# Revit family: Sink-Wall_Mount-Lavatory-KOHLER-Rêve-K-5148_1
name_source: partatom
category: Plumbing Fixtures
revit_build: Autodesk Revit 2015 (Build: 20140606_1530(x64)
units: mm (PartAtom-declared; Revit-internal decimal feet)

## types (6) — shared parameters
ADA Compliant = No
Assembly Code = D2010400
CW Connection = No
Cold Water Inlet = Cold Water Inlet
Date Modified = 4/5/2019
Default Elevation = 36"
Drain Included = No
HW Connection = No
Height = 6 5/16"
Hot Water Inlet = Hot Water Inlet
Length = 39 3/8"
Manufacturer = KOHLER Co.
MasterFormat 1995 = 15410
MasterFormat 2004 = 22.41.16
Material = Fireclay
Product Documentation Link = https://www.us.kohler.com
Product Name = Rêve
Product Page URL = http://www.us.kohler.com
URL = https://www.us.kohler.com
Vent Connection = No
Waste Connection = Yes
Waste Water Outlet = Waste Water Outlet
WaterSense Certified = No
Width = 18 5/16"

## per-type parameters (varying)
| type | Description | Faucet Hole Distance | Finish | Model | Type | Widespread Faucet Hole |
| Single Faucet Hole,0-White | 39 inch semi-pedestal bathroom sink with single faucet hole | 0" | Kohler-Fireclay-0-White | K-5148-1-0 | 1 | No |
| Single Faucet Hole,96-Biscuit | 39 inch semi-pedestal bathroom sink with single faucet hole | 0" | Kohler-Fireclay-96-Biscuit | K-5148-1-96 | 2 | No |
| Single Faucet Hole,47-Almond | 39 inch semi-pedestal bathroom sink with single faucet hole | 0" | Kohler-Fireclay-47-Almond | K-5148-1-47 | 3 | No |
| 8 inch Widespread Faucet Hole,0-White | 39 inch semi-pedestal bathroom sink with 8 inch widespread faucet holes | 8" | Kohler-Fireclay-0-White | K-5148-8-0 | 4 | Yes |
| 8 inch Widespread Faucet Hole,96-Biscuit | 39 inch semi-pedestal bathroom sink with 8 inch widespread faucet holes | 8" | Kohler-Fireclay-96-Biscuit | K-5148-8-96 | 5 | Yes |
| 8 inch Widespread Faucet Hole,47-Almond | 39 inch semi-pedestal bathroom sink with 8 inch widespread faucet holes | 8" | Kohler-Fireclay-47-Almond | K-5148-8-47 | 6 | Yes |

## geometry (parser evidence)
native form markers: Sweep x5
no freeform markers — native parametric forms only
